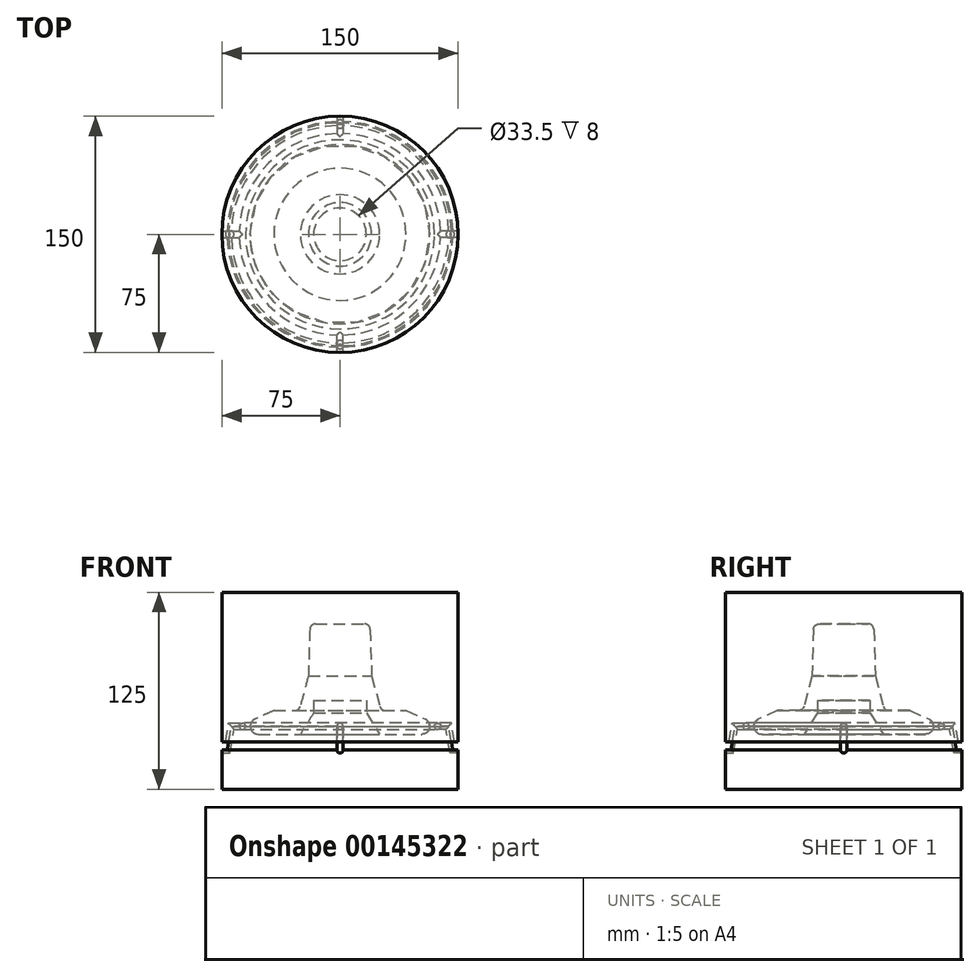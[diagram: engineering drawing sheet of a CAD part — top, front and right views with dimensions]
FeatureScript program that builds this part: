
annotation { "Feature Type Name" : "Feature", "Feature Type Description" : "" }
export const myFeature = defineFeature(function(context is Context, id is Id, definition is map)
    precondition{}
    {
        {
            var Q0;
            Q0=qCreatedBy(makeId("Front.planeOp"),FACE);
            var sketch = newSketch(context, id + "F0", { "sketchPlane" : qUnion([Q0])});
            skLineSegment(sketch, "E0.top", {"start": v(42, -35.55) * mm, "end": v(16.75, -35.55) * mm});
            skLineSegment(sketch, "E0.left", {"start": v(42, -20.55) * mm, "end": v(42, -35.55) * mm});
            skLineSegment(sketch, "E0.right", {"start": v(-42, -20.55) * mm, "end": v(-42, -35.55) * mm});
            skPoint(sketch, "E0.middle", {"position": v(0, 0) * mm});
            skLineSegment(sketch, "E1", {"start": v(0, -9.78) * mm, "end": v(0, -9.78) * mm});
            skPoint(sketch, "E1.endSnap0", {"position": v(0, -35.55) * mm});
            skLineSegment(sketch, "E2", {"start": v(-42, -20.55) * mm, "end": v(-28.69, -20.55) * mm});
            skPoint(sketch, "E3.middle", {"position": v(0, 1) * mm});
            skLineSegment(sketch, "E4", {"start": v(-19.16, 31.06) * mm, "end": v(-20.1, 1.45) * mm});
            skLineSegment(sketch, "E5", {"start": v(-20.1, 1.45) * mm, "end": v(-25.3, -17.96) * mm});
            skLineSegment(sketch, "E6.MirrorCS", {"start": v(20.1, 1.45) * mm, "end": v(26, -20.55) * mm});
            skLineSegment(sketch, "E7", {"start": v(-57, -20.55) * mm, "end": v(-57, -35.55) * mm});
            skLineSegment(sketch, "E8.MirrorCS", {"start": v(57, -20.55) * mm, "end": v(57, -35.55) * mm});
            skLineSegment(sketch, "E9", {"start": v(20.1, 1.45) * mm, "end": v(18.95, 34.45) * mm});
            skLineSegment(sketch, "E10", {"start": v(-15.66, 34.45) * mm, "end": v(18.95, 34.45) * mm});
            skLineSegment(sketch, "E11", {"start": v(-57, -30.55) * mm, "end": v(-42, -30.55) * mm});
            skPoint(sketch, "E12", {"position": v(-52, -30.55) * mm});
            skCircle(sketch, "E13", {"center": v(-52, -30.55) * mm, "radius": 5 * mm});
            skLineSegment(sketch, "E14", {"start": v(-42, -35.55) * mm, "end": v(-52, -35.55) * mm});
            skLineSegment(sketch, "E15", {"start": v(-42, -20.55) * mm, "end": v(-54.06, -26) * mm});
            skLineSegment(sketch, "E16", {"start": v(-16.75, -14.05) * mm, "end": v(16.75, -14.05) * mm});
            skPoint(sketch, "E17", {"position": v(0, -14.05) * mm});
            skLineSegment(sketch, "E18", {"start": v(-16.75, -14.05) * mm, "end": v(-16.75, -22.05) * mm});
            skLineSegment(sketch, "E19", {"start": v(16.75, -14.05) * mm, "end": v(16.75, -35.55) * mm});
            skPoint(sketch, "E20", {"position": v(-25.19, -35.55) * mm});
            skPoint(sketch, "E21", {"position": v(-16.75, -22.05) * mm});
            skLineSegment(sketch, "E22", {"start": v(-16.75, -22.05) * mm, "end": v(-25.19, -35.55) * mm});
            skLineSegment(sketch, "E23.trimOffspring", {"start": v(-25.19, -35.55) * mm, "end": v(-42, -35.55) * mm});
            skLineSegment(sketch, "E24.trimOffspring", {"start": v(16.75, -20.55) * mm, "end": v(42, -20.55) * mm});
            skPoint(sketch, "E25.visualSharp", {"position": v(-19.05, 34.45) * mm});
            skArc(sketch, "E25.filletArc", {"start": v(-15.66, 34.45) * mm, "mid": v(-18.1, 33.46) * mm, "end": v(-19.16, 31.06) * mm});
            skPoint(sketch, "E26.visualSharp", {"position": v(-26, -20.55) * mm});
            skArc(sketch, "E26.filletArc", {"start": v(-28.69, -20.55) * mm, "mid": v(-26.55, -19.83) * mm, "end": v(-25.3, -17.96) * mm});
            skLineSegment(sketch, "E27", {"start": v(0, -30.55) * mm, "end": v(0, 54.45) * mm});
            skLineSegment(sketch, "E28", {"start": v(0, 54.45) * mm, "end": v(-75, 54.45) * mm});
            skLineSegment(sketch, "E29", {"start": v(-75, 54.45) * mm, "end": v(-75, -70.55) * mm});
            skLineSegment(sketch, "E30", {"start": v(-75, -70.55) * mm, "end": v(0, -70.55) * mm});
            skLineSegment(sketch, "E31", {"start": v(0, -70.55) * mm, "end": v(0, -30.55) * mm});
            skLineSegment(sketch, "E32", {"start": v(0, -30.55) * mm, "end": v(-75, -30.55) * mm});
            skCircle(sketch, "E33", {"center": v(-62, -30.55) * mm, "radius": 2 * mm});
            skLineSegment(sketch, "E34", {"start": v(-75, -40.55) * mm, "end": v(-70.76, -40.55) * mm});
            skLineSegment(sketch, "E35", {"start": v(-75, -45.55) * mm, "end": v(-71.64, -45.55) * mm});
            skLineSegment(sketch, "E36", {"start": v(-71.64, -45.55) * mm, "end": v(-69, -30.55) * mm});
            skLineSegment(sketch, "E37", {"start": v(-62, -30.55) * mm, "end": v(-69, -30.55) * mm});
            skSolve(sketch);
        }
        {
            var Q0;
            {var subQ10=sQuery(id+"F0.wireOp",EDGE,"E2");Q0=makeQuery(id+"F0.imprint","IMPRINT",FACE,{"disambiguationData":[TD([[makeQuery(id+"F0.imprint","IMPRINT",EDGE,{"derivedFrom":subQ10}),-1.0]])]});}
            var Q1;
            {var subQ0=sQuery(id+"F0.wireOp",EDGE,"E15");Q1=makeQuery(id+"F0.imprint","IMPRINT",FACE,{"disambiguationData":[TD([[makeQuery(id+"F0.imprint","IMPRINT",EDGE,{"derivedFrom":subQ0}),1.0]])]});}
            var Q2;
            {var subQ0=sQuery(id+"F0.wireOp",EDGE,"E13");var subQ1=sQuery(id+"F0.wireOp",EDGE,"E11");var subQ2=makeQuery(id+"F0.imprint","INTERSECT",VERTEX,{"disambiguationData":[OD(0.0)],"derivedFrom":[subQ1,subQ0]});Q2=makeQuery(id+"F0.imprint","IMPRINT",FACE,{"disambiguationData":[TD([[makeQuery(id+"F0.imprint","IMPRINT",EDGE,{"disambiguationData":[TD([[subQ2,-1.0]])],"derivedFrom":subQ1}),1.0]])]});}
            var Q3;
            {var subQ0=sQuery(id+"F0.wireOp",EDGE,"E13");var subQ1=sQuery(id+"F0.wireOp",EDGE,"E11");var subQ2=makeQuery(id+"F0.imprint","INTERSECT",VERTEX,{"disambiguationData":[OD(0.0)],"derivedFrom":[subQ1,subQ0]});Q3=makeQuery(id+"F0.imprint","IMPRINT",FACE,{"disambiguationData":[TD([[makeQuery(id+"F0.imprint","IMPRINT",EDGE,{"disambiguationData":[TD([[subQ2,-1.0]])],"derivedFrom":subQ1}),-1.0]])]});}
            var Q4;
            {var subQ0=sQuery(id+"F0.wireOp",EDGE,"E14");Q4=makeQuery(id+"F0.imprint","IMPRINT",FACE,{"disambiguationData":[TD([[makeQuery(id+"F0.imprint","IMPRINT",EDGE,{"derivedFrom":subQ0}),-1.0]])]});}
            var Q5;
            {var subQ0=sQuery(id+"F0.wireOp",EDGE,"E13");var subQ1=makeQuery(id+"F0.imprint","INTERSECT",VERTEX,{"derivedFrom":[subQ0,sQuery(id+"F0.wireOp",EDGE,"E15")]});Q5=makeQuery(id+"F0.imprint","IMPRINT",FACE,{"disambiguationData":[TD([[makeQuery(id+"F0.imprint","IMPRINT",EDGE,{"disambiguationData":[TD([[subQ1,1.0]])],"derivedFrom":subQ0}),1.0]])]});}
            var Q6;
            {var subQ0=sQuery(id+"F0.wireOp",EDGE,"E13");var subQ1=makeQuery(id+"F0.imprint","INTERSECT",VERTEX,{"derivedFrom":[subQ0,sQuery(id+"F0.wireOp",EDGE,"E14")]});Q6=makeQuery(id+"F0.imprint","IMPRINT",FACE,{"disambiguationData":[TD([[makeQuery(id+"F0.imprint","IMPRINT",EDGE,{"disambiguationData":[TD([[subQ1,1.0]])],"derivedFrom":subQ0}),1.0]])]});}
            var Q7;
            {var subQ0=sQuery(id+"F0.wireOp",EDGE,"E23.trimOffspring");Q7=makeQuery(id+"F0.imprint","IMPRINT",FACE,{"disambiguationData":[TD([[makeQuery(id+"F0.imprint","IMPRINT",EDGE,{"derivedFrom":subQ0}),-1.0]])]});}
            var Q8;
            Q8=sQuery(id+"F0.wireOp",EDGE,"E27");
            revolve(context, id + "F1", {"entities" : qUnion([Q0, Q1, Q2, Q3, Q4, Q5, Q6, Q7]), "axis" : qUnion([Q8]), "revolveType" : RevolveType.FULL});
        }
        {
            var Q0;
            {var subQ15=sQuery(id+"F0.wireOp",EDGE,"E14");Q0=makeQuery(id+"F0.imprint","IMPRINT",FACE,{"disambiguationData":[TD([[makeQuery(id+"F0.imprint","IMPRINT",EDGE,{"derivedFrom":subQ15}),1.0]])]});}
            var Q1;
            {var subQ6=sQuery(id+"F0.wireOp",EDGE,"E18");Q1=makeQuery(id+"F0.imprint","IMPRINT",FACE,{"disambiguationData":[TD([[makeQuery(id+"F0.imprint","IMPRINT",EDGE,{"derivedFrom":subQ6}),1.0]])]});}
            var Q2;
            Q2=sQuery(id+"F0.wireOp",EDGE,"E27");
            revolve(context, id + "F2", {"entities" : qUnion([Q0, Q1]), "axis" : qUnion([Q2]), "revolveType" : RevolveType.FULL});
        }
        {
            var Q0;
            Q0=makeQuery(id+"F0.imprint","IMPRINT",FACE,{"disambiguationData":[TD([[makeQuery(id+"F0.imprint","IMPRINT",EDGE,{"derivedFrom":sQuery(id+"F0.wireOp",EDGE,"E2")}),1.0]])]});
            var Q1;
            {var subQ3=sQuery(id+"F0.wireOp",EDGE,"E34");Q1=makeQuery(id+"F0.imprint","IMPRINT",FACE,{"disambiguationData":[TD([[makeQuery(id+"F0.imprint","IMPRINT",EDGE,{"derivedFrom":subQ3}),1.0]])]});}
            var Q2;
            {var subQ0=sQuery(id+"F0.wireOp",EDGE,"E33");var subQ1=sQuery(id+"F0.wireOp",EDGE,"E32");var subQ2=makeQuery(id+"F0.imprint","INTERSECT",VERTEX,{"disambiguationData":[OD(0.0)],"derivedFrom":[subQ1,subQ0]});Q2=makeQuery(id+"F0.imprint","IMPRINT",FACE,{"disambiguationData":[TD([[makeQuery(id+"F0.imprint","IMPRINT",EDGE,{"disambiguationData":[TD([[subQ2,-1.0]])],"derivedFrom":subQ1}),-1.0]])]});}
            var Q3;
            Q3=sQuery(id+"F0.wireOp",EDGE,"E27");
            revolve(context, id + "F3", {"entities" : qUnion([Q0, Q1, Q2]), "axis" : qUnion([Q3]), "revolveType" : RevolveType.FULL});
        }
        {
            var Q0;
            Q0=qCreatedBy(makeId("Right.planeOp"),FACE);
            cPlane(context, id + "F4", {"entities" : qUnion([Q0]), "cplaneType" : CPlaneType.OFFSET, "offset" : 75 * mm, "oppositeDirection" : true, "width" : 150 * mm, "height" : 150 * mm});
        }
        {
            var Q0;
            Q0=qCreatedBy(id+"F4.planeOp",FACE);
            var sketch = newSketch(context, id + "F5", { "sketchPlane" : qUnion([Q0])});
            skPoint(sketch, "E38", {"position": v(0, -45.55) * mm});
            skCircle(sketch, "E39", {"center": v(0, -45.55) * mm, "radius": 2 * mm});
            skSolve(sketch);
        }
        {
            var Q0;
            Q0=makeQuery(id+"F5.imprint","IMPRINT",FACE,{"disambiguationData":[TD([[makeQuery(id+"F5.imprint","IMPRINT",EDGE,{"derivedFrom":sQuery(id+"F5.wireOp",EDGE,"E39")}),1.0]])]});
            var Q1;
            Q1=sQuery(id+"F0.wireOp",EDGE,"E35");
            var Q2;
            Q2=sQuery(id+"F0.wireOp",EDGE,"E36");
            var Q3;
            Q3=sQuery(id+"F0.wireOp",EDGE,"E37");
            sweep(context, id + "F6", {"operationType" : NewBodyOperationType.REMOVE, "profiles" : qUnion([Q0]), "path" : qUnion([Q1, Q2, Q3])});
        }
        {
            var Q0;
            Q0=makeQuery(id+"F6.boolean.opBoolean","COPY",FACE,{"derivedFrom":makeQuery(id+"F6.opSweep","SWEPT_FACE",FACE,{"disambiguationData":[OSD([sQuery(id+"F0.wireOp",EDGE,"E35"),sQuery(id+"F5.wireOp",EDGE,"E39")])]})});
            var Q1;
            Q1=makeQuery(id+"F6.boolean.opBoolean","COPY",FACE,{"derivedFrom":makeQuery(id+"F6.opSweep","SWEPT_FACE",FACE,{"disambiguationData":[OSD([sQuery(id+"F0.wireOp",EDGE,"E36"),sQuery(id+"F5.wireOp",EDGE,"E39")])]})});
            var Q2;
            Q2=makeQuery(id+"F6.boolean.opBoolean","COPY",FACE,{"derivedFrom":makeQuery(id+"F6.opSweep","SWEPT_FACE",FACE,{"disambiguationData":[OSD([sQuery(id+"F0.wireOp",EDGE,"E37"),sQuery(id+"F5.wireOp",EDGE,"E39")])]})});
            var Q3;
            Q3=sQuery(id+"F0.wireOp",EDGE,"E27");
            circularPattern(context, id + "F7", {"patternType" : PatternType.FACE, "faces" : qUnion([Q0, Q1, Q2]), "axis" : qUnion([Q3]), "angle" : 90 * degree, "instanceCount" : 4});
        }
    });
